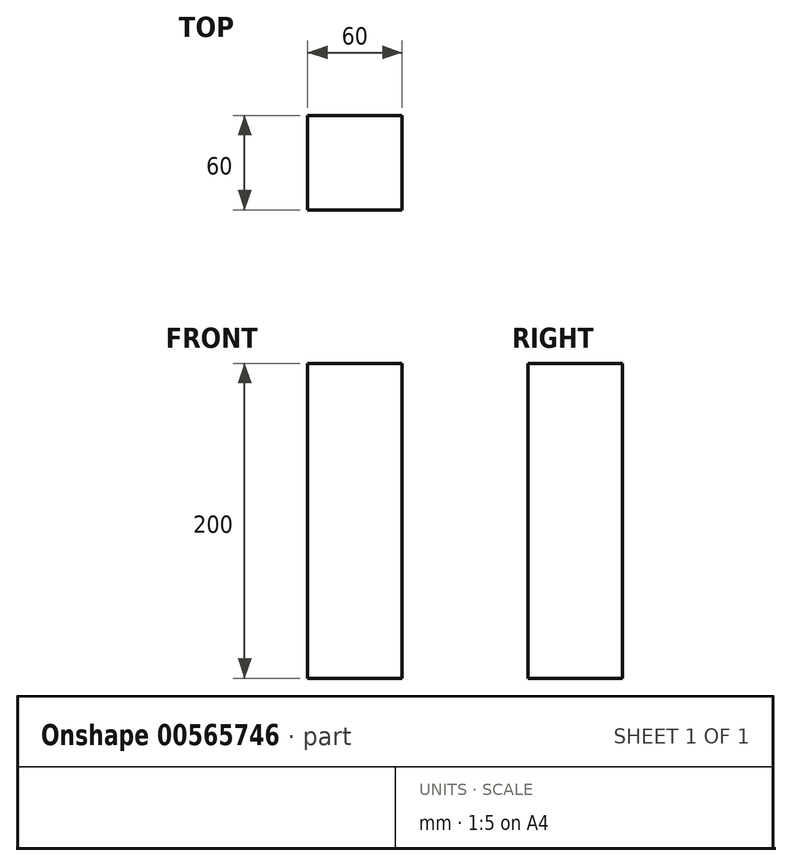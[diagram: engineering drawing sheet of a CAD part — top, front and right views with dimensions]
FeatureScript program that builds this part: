
annotation { "Feature Type Name" : "Feature", "Feature Type Description" : "" }
export const myFeature = defineFeature(function(context is Context, id is Id, definition is map)
    precondition{}
    {
        {
            var Q0;
            Q0=qCreatedBy(makeId("Top.planeOp"),FACE);
            var sketch = newSketch(context, id + "F0", { "sketchPlane" : qUnion([Q0])});
            skLineSegment(sketch, "E0.bottom", {"start": v(30, 30) * mm, "end": v(-30, 30) * mm});
            skLineSegment(sketch, "E0.top", {"start": v(30, -30) * mm, "end": v(-30, -30) * mm});
            skLineSegment(sketch, "E0.left", {"start": v(30, 30) * mm, "end": v(30, -30) * mm});
            skLineSegment(sketch, "E0.right", {"start": v(-30, 30) * mm, "end": v(-30, -30) * mm});
            skPoint(sketch, "E0.middle", {"position": v(0, 0) * mm});
            skSolve(sketch);
        }
        {
            var Q0;
            Q0 = qSketchRegion(id + "F0", true);
            extrude(context, id + "F1", {"entities" : qUnion([Q0]), "depth" : 200 * mm, "offsetDistance" : 25 * mm});
        }
    });
